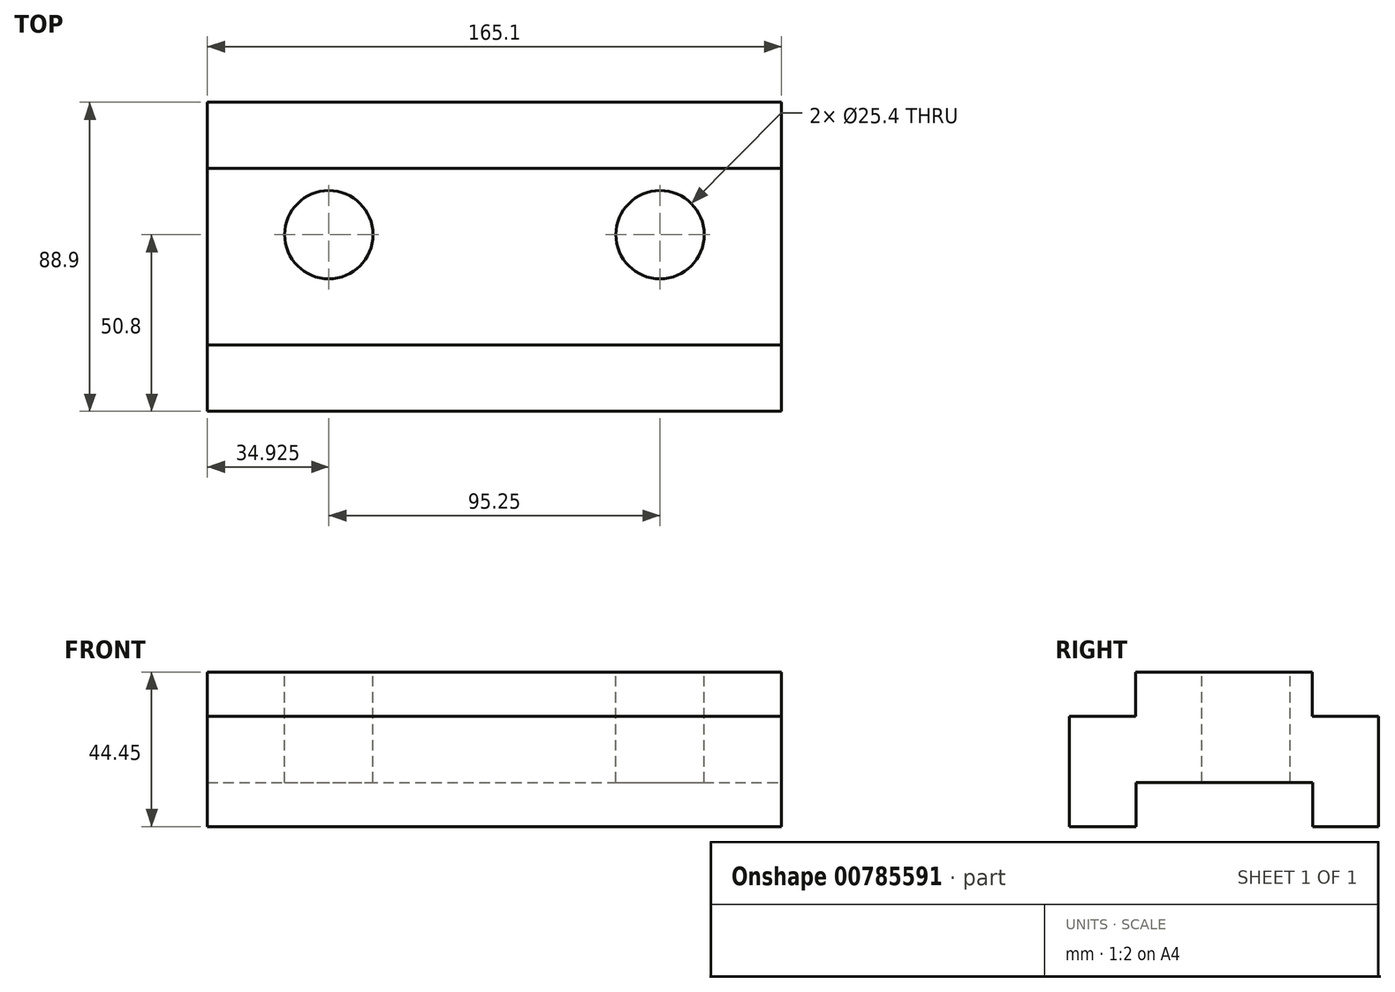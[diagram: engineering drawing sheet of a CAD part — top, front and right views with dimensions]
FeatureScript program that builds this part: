
annotation { "Feature Type Name" : "Feature", "Feature Type Description" : "" }
export const myFeature = defineFeature(function(context is Context, id is Id, definition is map)
    precondition{}
    {
        {
            var Q0;
            Q0=qCreatedBy(makeId("Front.planeOp"),FACE);
            var sketch = newSketch(context, id + "F0", { "sketchPlane" : qUnion([Q0])});
            skLineSegment(sketch, "E0.bottom", {"start": v(0, 0) * mm, "end": v(165.1, 0) * mm});
            skLineSegment(sketch, "E0.top", {"start": v(0, 44.45) * mm, "end": v(165.1, 44.45) * mm});
            skLineSegment(sketch, "E0.left", {"start": v(0, 0) * mm, "end": v(0, 44.45) * mm});
            skLineSegment(sketch, "E0.right", {"start": v(165.1, 0) * mm, "end": v(165.1, 44.45) * mm});
            skSolve(sketch);
        }
        {
            var Q0;
            Q0=makeQuery(id+"F0.imprint","IMPRINT",FACE,{"disambiguationData":[TD([[makeQuery(id+"F0.imprint","IMPRINT",EDGE,{"derivedFrom":sQuery(id+"F0.wireOp",EDGE,"E0.bottom")}),1.0]])]});
            extrude(context, id + "F1", {"entities" : qUnion([Q0]), "oppositeDirection" : true, "depth" : 88.9 * mm, "offsetDistance" : 25.4 * mm});
        }
        {
            var Q0;
            Q0=makeQuery(id+"F1.opExtrude","SWEPT_FACE",FACE,{"disambiguationData":[OSD([sQuery(id+"F0.wireOp",EDGE,"E0.right")])]});
            var sketch = newSketch(context, id + "F2", { "sketchPlane" : qUnion([Q0])});
            skLineSegment(sketch, "E1.bottom", {"start": v(0, 31.75) * mm, "end": v(19.05, 31.75) * mm});
            skLineSegment(sketch, "E1.top", {"start": v(0, 44.45) * mm, "end": v(19.05, 44.45) * mm});
            skLineSegment(sketch, "E1.left", {"start": v(0, 31.75) * mm, "end": v(0, 44.45) * mm});
            skLineSegment(sketch, "E1.right", {"start": v(19.05, 31.75) * mm, "end": v(19.05, 44.45) * mm});
            skLineSegment(sketch, "E2.bottom", {"start": v(88.9, 31.75) * mm, "end": v(69.85, 31.75) * mm});
            skLineSegment(sketch, "E2.top", {"start": v(88.9, 44.45) * mm, "end": v(69.85, 44.45) * mm});
            skLineSegment(sketch, "E2.left", {"start": v(88.9, 31.75) * mm, "end": v(88.9, 44.45) * mm});
            skLineSegment(sketch, "E2.right", {"start": v(69.85, 31.75) * mm, "end": v(69.85, 44.45) * mm});
            skSolve(sketch);
        }
        {
            var Q0;
            Q0=makeQuery(id+"F2.imprint","IMPRINT",FACE,{"disambiguationData":[TD([[makeQuery(id+"F2.imprint","IMPRINT",EDGE,{"derivedFrom":sQuery(id+"F2.wireOp",EDGE,"E1.bottom")}),1.0]])]});
            extrude(context, id + "F3", {"entities" : qUnion([Q0]), "operationType" : NewBodyOperationType.REMOVE, "oppositeDirection" : true, "depth" : 254 * mm, "offsetDistance" : 25.4 * mm});
        }
        {
            var Q0;
            Q0=makeQuery(id+"F1.opExtrude","SWEPT_FACE",FACE,{"disambiguationData":[OSD([sQuery(id+"F0.wireOp",EDGE,"E0.right")])]});
            var sketch = newSketch(context, id + "F4", { "sketchPlane" : qUnion([Q0])});
            skLineSegment(sketch, "E3.bottom", {"start": v(88.9, 31.75) * mm, "end": v(69.85, 31.75) * mm});
            skLineSegment(sketch, "E3.top", {"start": v(88.9, 44.45) * mm, "end": v(69.85, 44.45) * mm});
            skLineSegment(sketch, "E3.left", {"start": v(88.9, 31.75) * mm, "end": v(88.9, 44.45) * mm});
            skLineSegment(sketch, "E3.right", {"start": v(69.85, 31.75) * mm, "end": v(69.85, 44.45) * mm});
            skSolve(sketch);
        }
        {
            var Q0;
            Q0=makeQuery(id+"F4.imprint","IMPRINT",FACE,{"disambiguationData":[TD([[makeQuery(id+"F4.imprint","IMPRINT",EDGE,{"derivedFrom":sQuery(id+"F4.wireOp",EDGE,"E3.bottom")}),-1.0]])]});
            extrude(context, id + "F5", {"entities" : qUnion([Q0]), "operationType" : NewBodyOperationType.REMOVE, "oppositeDirection" : true, "depth" : 254 * mm, "offsetDistance" : 25.4 * mm});
        }
        {
            var Q0;
            Q0=makeQuery(id+"F1.opExtrude","SWEPT_FACE",FACE,{"disambiguationData":[OSD([sQuery(id+"F0.wireOp",EDGE,"E0.right")])]});
            var sketch = newSketch(context, id + "F6", { "sketchPlane" : qUnion([Q0])});
            skLineSegment(sketch, "E4.bottom", {"start": v(19.18, 0) * mm, "end": v(69.98, 0) * mm});
            skLineSegment(sketch, "E4.top", {"start": v(19.18, 12.7) * mm, "end": v(69.98, 12.7) * mm});
            skLineSegment(sketch, "E4.left", {"start": v(19.18, 0) * mm, "end": v(19.18, 12.7) * mm});
            skLineSegment(sketch, "E4.right", {"start": v(69.98, 0) * mm, "end": v(69.98, 12.7) * mm});
            skSolve(sketch);
        }
        {
            var Q0;
            Q0=makeQuery(id+"F6.imprint","IMPRINT",FACE,{"disambiguationData":[TD([[makeQuery(id+"F6.imprint","IMPRINT",EDGE,{"derivedFrom":sQuery(id+"F6.wireOp",EDGE,"E4.bottom")}),-1.0]])]});
            extrude(context, id + "F7", {"entities" : qUnion([Q0]), "operationType" : NewBodyOperationType.REMOVE, "oppositeDirection" : true, "depth" : 254 * mm, "offsetDistance" : 25.4 * mm});
        }
        {
            var Q0;
            Q0=makeQuery(id+"F1.opExtrude","SWEPT_FACE",FACE,{"disambiguationData":[OSD([sQuery(id+"F0.wireOp",EDGE,"E0.top")])]});
            var sketch = newSketch(context, id + "F8", { "sketchPlane" : qUnion([Q0])});
            skLineSegment(sketch, "E5", {"start": v(0, 69.85) * mm, "end": v(34.93, 69.85) * mm});
            skLineSegment(sketch, "E6", {"start": v(34.93, 69.85) * mm, "end": v(34.93, 50.8) * mm});
            skSolve(sketch);
        }
        {
            var Q0;
            Q0=sQuery(id+"F8.wireOp",VERTEX,"E6.end");
            var Q1;
            Q1=makeQuery(id+"F1.opExtrude","SWEPT_BODY",BODY,{"disambiguationData":[OSD([sQuery(id+"F0.wireOp",EDGE,"E0.bottom"),sQuery(id+"F0.wireOp",EDGE,"E0.top"),sQuery(id+"F0.wireOp",EDGE,"E0.left"),sQuery(id+"F0.wireOp",EDGE,"E0.right")])]});
            hole(context, id + "F9", {"style" : HoleStyle.SIMPLE, "endStyle" : HoleEndStyle.THROUGH, "holeDiameter" : 25.4 * mm, "majorDiameter" : 6.35 * mm, "isTappedThrough" : true, "tappedDepth" : 12.7 * mm, "tapClearance" : 3, "locations" : qUnion([Q0]), "scope" : qUnion([Q1])});
        }
        {
            var Q0;
            Q0=makeQuery(id+"F1.opExtrude","SWEPT_FACE",FACE,{"disambiguationData":[OSD([sQuery(id+"F0.wireOp",EDGE,"E0.top")])]});
            var sketch = newSketch(context, id + "F10", { "sketchPlane" : qUnion([Q0])});
            skLineSegment(sketch, "E7", {"start": v(34.93, 50.8) * mm, "end": v(130.18, 50.8) * mm});
            skSolve(sketch);
        }
        {
            var Q0;
            Q0=sQuery(id+"F10.wireOp",VERTEX,"E7.end");
            var Q1;
            Q1=makeQuery(id+"F1.opExtrude","SWEPT_BODY",BODY,{"disambiguationData":[OSD([sQuery(id+"F0.wireOp",EDGE,"E0.bottom"),sQuery(id+"F0.wireOp",EDGE,"E0.top"),sQuery(id+"F0.wireOp",EDGE,"E0.left"),sQuery(id+"F0.wireOp",EDGE,"E0.right")])]});
            hole(context, id + "F11", {"style" : HoleStyle.SIMPLE, "endStyle" : HoleEndStyle.THROUGH, "holeDiameter" : 25.4 * mm, "majorDiameter" : 6.35 * mm, "isTappedThrough" : true, "tappedDepth" : 12.7 * mm, "tapClearance" : 3, "locations" : qUnion([Q0]), "scope" : qUnion([Q1])});
        }
    });
